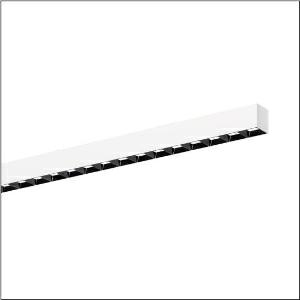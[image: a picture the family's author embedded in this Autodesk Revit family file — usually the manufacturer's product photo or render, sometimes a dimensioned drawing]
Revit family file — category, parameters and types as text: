
# Revit family: silica_r__21_51mx24da44wb_4eb4
name_source: partatom
category: Lighting Fixtures
units: mm (PartAtom-declared; Revit-internal decimal feet)

## family parameters
Cut with Voids When Loaded = No
Host = Face
Light Source = No
Part Type = Normal
Room Calculation Point = No
Round Connector Dimension = Use Diameter
Shared = No

## types (1)
- --- (1 x LED, 4320 lm, 30 W, 4000K)
    Apparent Load = 30 VA
    CIE Flux Codes = 74 94 99 100 100
    Color Rendering = 80
    Color Temperature = 4000K
    Default Elevation = 1800 mm
    Description = Silica® 21, office luminaire, primary light control with darklight reflector, of PMMA, black, CAT 2 (L<= 3000cd/m²), light emission: direct distribution, primary light characteristic: asymmetric, installation type: surface-mounted, LED, rated luminous flux: 4.320lm, luminous efficacy: 144lm/W, light colour: 840, colour temperature: 4000K, with terminal, 3+2-pole, max. 2.5mm², mains connection: 220..240V, AC, 50/60Hz, rated input power: 30W, luminaire housing, of aluminium, traffic white (RAL 9016), length: 1.204mm, width: 53mm, height: 53mm, protection rating (complete): IP20, insulation class (complete): insulation class I (protective earthing), certification: CE, permissible operating ambient temperature: 0..+35°C, standard: EN 50419, packaging unit: 1 piece
    Height = 0 mm  [stored 0 ft]
    Lamp = 1 x LED
    Lamp Light Flux = 4320 lm
    Lamp Power = 30 W
    Lamp count = 1
    Length = 1204 mm
    Luminous efficacy = 144 lm/W
    Manufacturer = Siteco
    ModVariant = No
    Model = 51MX24DA44WB
    Mounting Place = Ceiling
    Mounting Type = Recessed
    Number of Poles = 1
    OnlyDefault = Yes
    Power Factor = 1
    Product Name = Silica® 21
    Product group = office luminaire | ceiling recessed
    ProductGroupID = 401
    Protection Class = Protection class I
    Protection Degree = IP 20
    RLX_Detail_Level = 1
    RLX_Emergency_Light_Flux = 0 lm
    RLX_Emergency_Type = 0
    RLX_Emergency_Type_DB = No
    RlxData = <blob elided: 41377 chars, md5=0b871e7c>
    Socket = socket
    Standby Power = 0 W
    System Light Flux = 4320 lm
    System Power = 30 W
    Type Comments = factory setting: luminous flux: 100 % | dim-lin: 254 | 418 mA
    Type Image = l_1297779.jpg
    URL = http://relux.com
    VarID = @adj_053981
    Voltage = 0 V
    Weight = 0.00 kg
    Width = 53 mm

note: [stored X ft] marks values corroborated as IEEE doubles in the binary element streams (Revit-internal decimal feet)

## geometry (parser evidence)
native form markers: Blend x4, Sweep x11
no freeform markers — native parametric forms only
